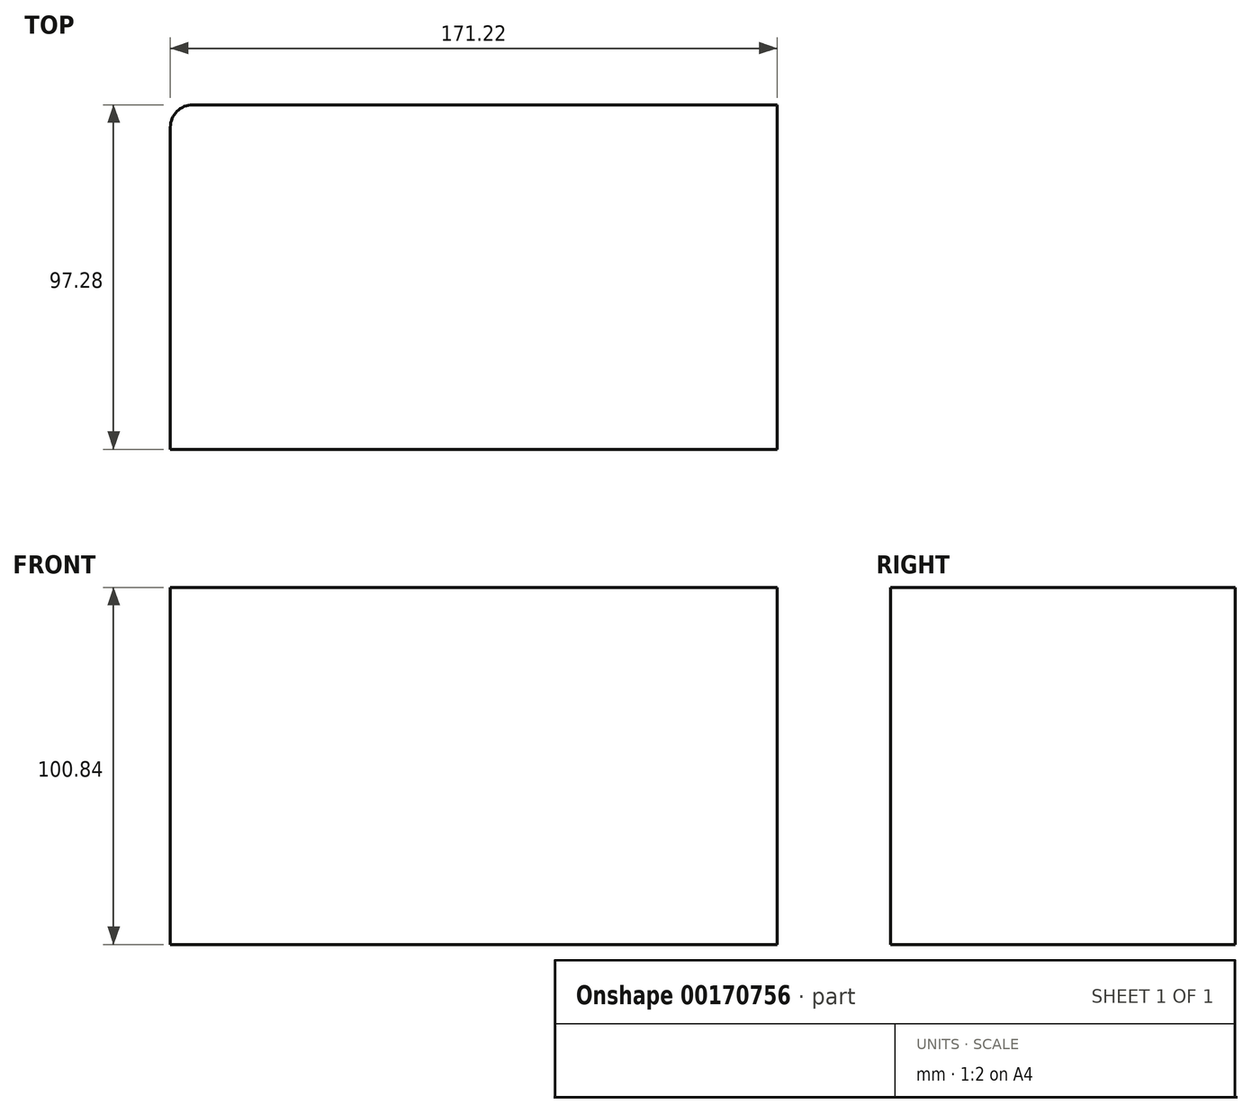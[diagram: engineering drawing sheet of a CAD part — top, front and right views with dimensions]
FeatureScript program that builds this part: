
annotation { "Feature Type Name" : "Feature", "Feature Type Description" : "" }
export const myFeature = defineFeature(function(context is Context, id is Id, definition is map)
    precondition{}
    {
        {
            var Q0;
            Q0=qCreatedBy(makeId("Top.planeOp"),FACE);
            var sketch = newSketch(context, id + "F0", { "sketchPlane" : qUnion([Q0])});
            skLineSegment(sketch, "E0.bottom", {"start": v(85.61, -48.64) * mm, "end": v(-85.61, -48.64) * mm});
            skLineSegment(sketch, "E0.top", {"start": v(85.61, 48.64) * mm, "end": v(-79.26, 48.64) * mm});
            skLineSegment(sketch, "E0.left", {"start": v(85.61, -48.64) * mm, "end": v(85.61, 48.64) * mm});
            skLineSegment(sketch, "E0.right", {"start": v(-85.61, -48.64) * mm, "end": v(-85.61, 42.3) * mm});
            skPoint(sketch, "E0.middle", {"position": v(0, 0) * mm});
            skPoint(sketch, "E1.visualSharp", {"position": v(-85.61, 48.64) * mm});
            skArc(sketch, "E1.filletArc", {"start": v(-79.26, 48.64) * mm, "mid": v(-83.75, 46.78) * mm, "end": v(-85.61, 42.3) * mm});
            skSolve(sketch);
        }
        {
            var Q0;
            Q0=makeQuery(id+"F0.imprint","IMPRINT",FACE,{"disambiguationData":[TD([[makeQuery(id+"F0.imprint","IMPRINT",EDGE,{"derivedFrom":sQuery(id+"F0.wireOp",EDGE,"E0.bottom")}),-1.0]])]});
            extrude(context, id + "F1", {"entities" : qUnion([Q0]), "depth" : 100.84 * mm});
        }
    });
